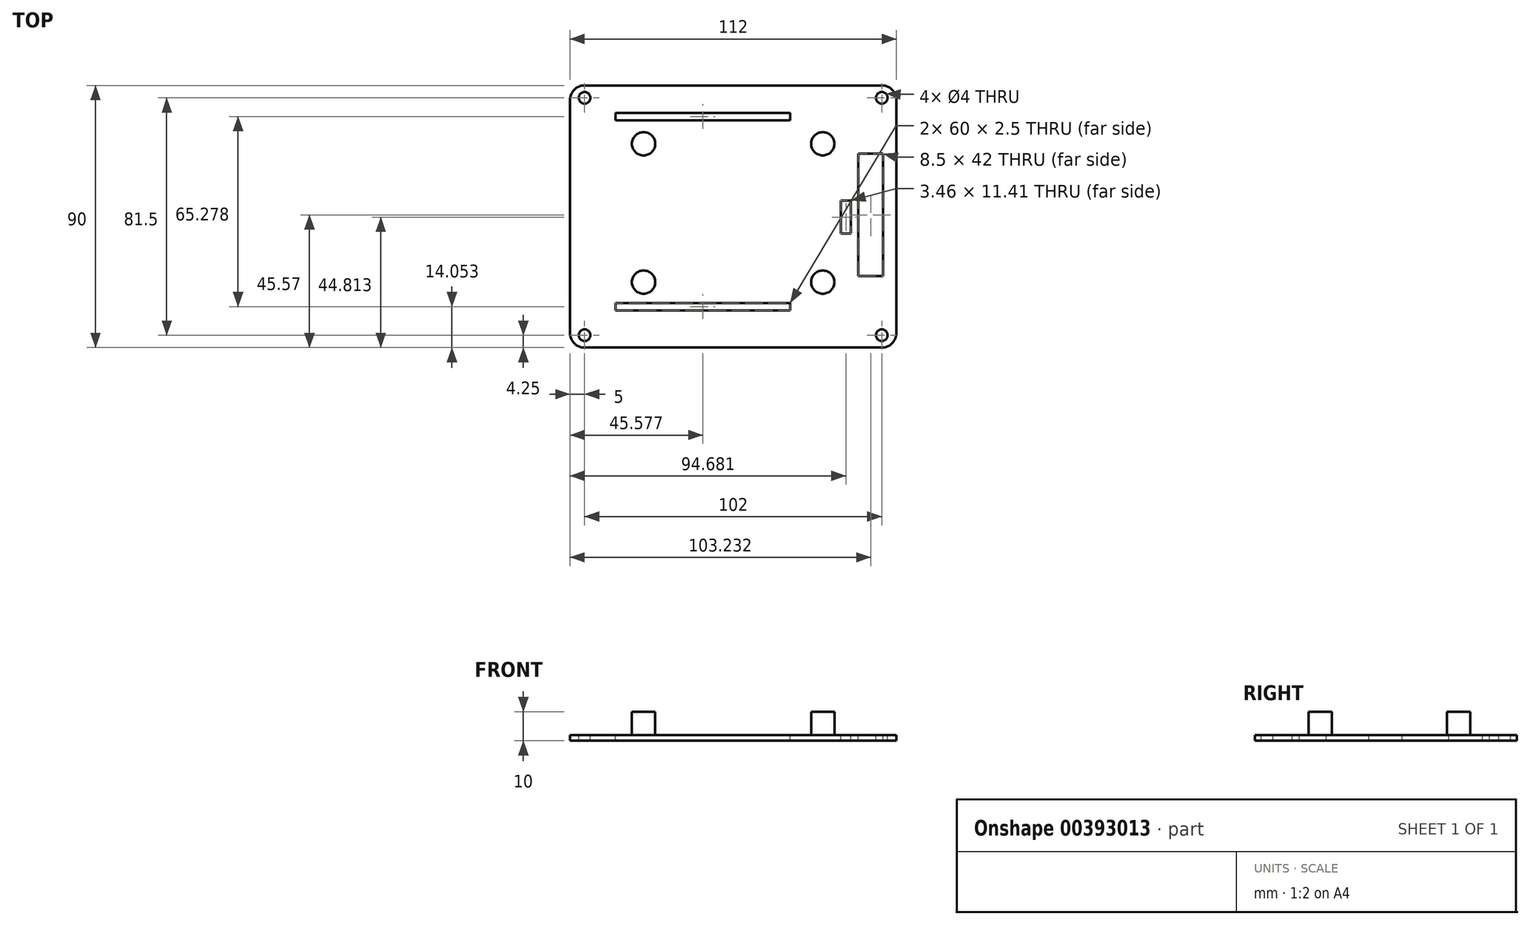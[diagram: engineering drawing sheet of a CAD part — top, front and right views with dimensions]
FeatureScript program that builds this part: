
annotation { "Feature Type Name" : "Feature", "Feature Type Description" : "" }
export const myFeature = defineFeature(function(context is Context, id is Id, definition is map)
    precondition{}
    {
        {
            var Q0;
            Q0=qCreatedBy(makeId("Top.planeOp"),FACE);
            var sketch = newSketch(context, id + "F0", { "sketchPlane" : qUnion([Q0])});
            skLineSegment(sketch, "E0.bottom", {"start": v(51, 45) * mm, "end": v(-51, 45) * mm});
            skLineSegment(sketch, "E0.top", {"start": v(51, -45) * mm, "end": v(-51, -45) * mm});
            skLineSegment(sketch, "E0.left", {"start": v(56, 40) * mm, "end": v(56, -40) * mm});
            skLineSegment(sketch, "E0.right", {"start": v(-56, 40) * mm, "end": v(-56, -40) * mm});
            skPoint(sketch, "E0.middle", {"position": v(0, 0) * mm});
            skPoint(sketch, "E1.visualSharp", {"position": v(56, 45) * mm});
            skArc(sketch, "E1.filletArc", {"start": v(56, 40) * mm, "mid": v(54.54, 43.54) * mm, "end": v(51, 45) * mm});
            skPoint(sketch, "E2.visualSharp", {"position": v(56, -45) * mm});
            skArc(sketch, "E2.filletArc", {"start": v(51, -45) * mm, "mid": v(54.54, -43.54) * mm, "end": v(56, -40) * mm});
            skPoint(sketch, "E3.visualSharp", {"position": v(-56, -45) * mm});
            skArc(sketch, "E3.filletArc", {"start": v(-56, -40) * mm, "mid": v(-54.54, -43.54) * mm, "end": v(-51, -45) * mm});
            skPoint(sketch, "E4.visualSharp", {"position": v(-56, 45) * mm});
            skArc(sketch, "E4.filletArc", {"start": v(-51, 45) * mm, "mid": v(-54.54, 43.54) * mm, "end": v(-56, 40) * mm});
            skSolve(sketch);
        }
        {
            var Q0;
            Q0 = qSketchRegion(id + "F0", true);
            extrude(context, id + "F1", {"entities" : qUnion([Q0]), "depth" : 2 * mm, "offsetDistance" : 25 * mm});
        }
        {
            var Q0;
            Q0=makeQuery(id+"F1.opExtrude","CAP_FACE",FACE,{"disambiguationData":[OSD([sQuery(id+"F0.wireOp",EDGE,"E0.bottom"),sQuery(id+"F0.wireOp",EDGE,"E0.top"),sQuery(id+"F0.wireOp",EDGE,"E0.left"),sQuery(id+"F0.wireOp",EDGE,"E0.right"),sQuery(id+"F0.wireOp",EDGE,"E1.filletArc"),sQuery(id+"F0.wireOp",EDGE,"E2.filletArc"),sQuery(id+"F0.wireOp",EDGE,"E3.filletArc"),sQuery(id+"F0.wireOp",EDGE,"E4.filletArc")])],"isStart":false});
            var sketch = newSketch(context, id + "F2", { "sketchPlane" : qUnion([Q0])});
            skLineSegment(sketch, "E5.bottom", {"start": v(42.98, 21.57) * mm, "end": v(51.48, 21.57) * mm});
            skLineSegment(sketch, "E5.top", {"start": v(42.98, -20.43) * mm, "end": v(51.48, -20.43) * mm});
            skLineSegment(sketch, "E5.left", {"start": v(42.98, 21.57) * mm, "end": v(42.98, -20.43) * mm});
            skLineSegment(sketch, "E5.right", {"start": v(51.48, 21.57) * mm, "end": v(51.48, -20.43) * mm});
            skSolve(sketch);
        }
        {
            var Q0;
            Q0 = qSketchRegion(id + "F2", true);
            extrude(context, id + "F3", {"entities" : qUnion([Q0]), "operationType" : NewBodyOperationType.REMOVE, "oppositeDirection" : true, "depth" : 25 * mm, "offsetDistance" : 25 * mm});
        }
        {
            var Q0;
            Q0=makeQuery(id+"F1.opExtrude","CAP_FACE",FACE,{"disambiguationData":[OSD([sQuery(id+"F0.wireOp",EDGE,"E0.bottom"),sQuery(id+"F0.wireOp",EDGE,"E0.top"),sQuery(id+"F0.wireOp",EDGE,"E0.left"),sQuery(id+"F0.wireOp",EDGE,"E0.right"),sQuery(id+"F0.wireOp",EDGE,"E1.filletArc"),sQuery(id+"F0.wireOp",EDGE,"E2.filletArc"),sQuery(id+"F0.wireOp",EDGE,"E3.filletArc"),sQuery(id+"F0.wireOp",EDGE,"E4.filletArc")])],"isStart":false});
            var sketch = newSketch(context, id + "F4", { "sketchPlane" : qUnion([Q0])});
            skLineSegment(sketch, "E6.bottom", {"start": v(51, 40.75) * mm, "end": v(-51, 40.75) * mm});
            skLineSegment(sketch, "E6.top", {"start": v(51, -40.75) * mm, "end": v(-51, -40.75) * mm});
            skLineSegment(sketch, "E6.left", {"start": v(51, 40.75) * mm, "end": v(51, -40.75) * mm});
            skLineSegment(sketch, "E6.right", {"start": v(-51, 40.75) * mm, "end": v(-51, -40.75) * mm});
            skPoint(sketch, "E6.middle", {"position": v(0, 0) * mm});
            skCircle(sketch, "E7", {"center": v(-51, 40.75) * mm, "radius": 2 * mm});
            skCircle(sketch, "E8", {"center": v(51, 40.75) * mm, "radius": 2 * mm});
            skCircle(sketch, "E9", {"center": v(51, -40.75) * mm, "radius": 2 * mm});
            skCircle(sketch, "E10", {"center": v(-51, -40.75) * mm, "radius": 2 * mm});
            skSolve(sketch);
        }
        {
            var Q0;
            Q0=makeQuery(id+"F4.imprint","IMPRINT",FACE,{"disambiguationData":[TD([[makeQuery(id+"F4.imprint","IMPRINT",EDGE,{"derivedFrom":makeQuery(id+"F3.boolean.opBoolean","COPY",EDGE,{"derivedFrom":makeQuery(id+"F3.opExtrude","CAP_EDGE",EDGE,{"disambiguationData":[OSD([sQuery(id+"F2.wireOp",EDGE,"E5.bottom")])],"isStart":true})})}),-1.0]])]});
            var Q1;
            {var subQ0=sQuery(id+"F4.wireOp",EDGE,"E6.left");var subQ1=sQuery(id+"F4.wireOp",EDGE,"E6.bottom");var subQ2=makeQuery(id+"F4.imprint","INTERSECT",VERTEX,{"derivedFrom":[subQ1,subQ0]});Q1=makeQuery(id+"F4.imprint","IMPRINT",FACE,{"disambiguationData":[TD([[makeQuery(id+"F4.imprint","IMPRINT",EDGE,{"disambiguationData":[TD([[subQ2,-1.0]])],"derivedFrom":subQ1}),1.0]])]});}
            var Q2;
            {var subQ0=sQuery(id+"F4.wireOp",EDGE,"E6.left");var subQ1=sQuery(id+"F4.wireOp",EDGE,"E6.bottom");var subQ2=makeQuery(id+"F4.imprint","INTERSECT",VERTEX,{"derivedFrom":[subQ1,subQ0]});Q2=makeQuery(id+"F4.imprint","IMPRINT",FACE,{"disambiguationData":[TD([[makeQuery(id+"F4.imprint","IMPRINT",EDGE,{"disambiguationData":[TD([[subQ2,-1.0]])],"derivedFrom":subQ1}),-1.0]])]});}
            var Q3;
            {var subQ0=sQuery(id+"F4.wireOp",EDGE,"E6.right");var subQ1=sQuery(id+"F4.wireOp",EDGE,"E6.bottom");var subQ2=makeQuery(id+"F4.imprint","INTERSECT",VERTEX,{"derivedFrom":[subQ1,subQ0]});Q3=makeQuery(id+"F4.imprint","IMPRINT",FACE,{"disambiguationData":[TD([[makeQuery(id+"F4.imprint","IMPRINT",EDGE,{"disambiguationData":[TD([[subQ2,1.0]])],"derivedFrom":subQ1}),-1.0]])]});}
            var Q4;
            {var subQ0=sQuery(id+"F4.wireOp",EDGE,"E6.right");var subQ1=sQuery(id+"F4.wireOp",EDGE,"E6.bottom");var subQ2=makeQuery(id+"F4.imprint","INTERSECT",VERTEX,{"derivedFrom":[subQ1,subQ0]});Q4=makeQuery(id+"F4.imprint","IMPRINT",FACE,{"disambiguationData":[TD([[makeQuery(id+"F4.imprint","IMPRINT",EDGE,{"disambiguationData":[TD([[subQ2,1.0]])],"derivedFrom":subQ1}),1.0]])]});}
            var Q5;
            {var subQ0=sQuery(id+"F4.wireOp",EDGE,"E6.left");var subQ1=sQuery(id+"F4.wireOp",EDGE,"E6.top");var subQ2=makeQuery(id+"F4.imprint","INTERSECT",VERTEX,{"derivedFrom":[subQ1,subQ0]});Q5=makeQuery(id+"F4.imprint","IMPRINT",FACE,{"disambiguationData":[TD([[makeQuery(id+"F4.imprint","IMPRINT",EDGE,{"disambiguationData":[TD([[subQ2,-1.0]])],"derivedFrom":subQ1}),-1.0]])]});}
            var Q6;
            {var subQ0=sQuery(id+"F4.wireOp",EDGE,"E6.left");var subQ1=sQuery(id+"F4.wireOp",EDGE,"E6.top");var subQ2=makeQuery(id+"F4.imprint","INTERSECT",VERTEX,{"derivedFrom":[subQ1,subQ0]});Q6=makeQuery(id+"F4.imprint","IMPRINT",FACE,{"disambiguationData":[TD([[makeQuery(id+"F4.imprint","IMPRINT",EDGE,{"disambiguationData":[TD([[subQ2,-1.0]])],"derivedFrom":subQ1}),1.0]])]});}
            var Q7;
            {var subQ0=sQuery(id+"F4.wireOp",EDGE,"E6.right");var subQ1=sQuery(id+"F4.wireOp",EDGE,"E6.top");var subQ2=makeQuery(id+"F4.imprint","INTERSECT",VERTEX,{"derivedFrom":[subQ1,subQ0]});Q7=makeQuery(id+"F4.imprint","IMPRINT",FACE,{"disambiguationData":[TD([[makeQuery(id+"F4.imprint","IMPRINT",EDGE,{"disambiguationData":[TD([[subQ2,1.0]])],"derivedFrom":subQ1}),-1.0]])]});}
            var Q8;
            {var subQ0=sQuery(id+"F4.wireOp",EDGE,"E6.right");var subQ1=sQuery(id+"F4.wireOp",EDGE,"E6.top");var subQ2=makeQuery(id+"F4.imprint","INTERSECT",VERTEX,{"derivedFrom":[subQ1,subQ0]});Q8=makeQuery(id+"F4.imprint","IMPRINT",FACE,{"disambiguationData":[TD([[makeQuery(id+"F4.imprint","IMPRINT",EDGE,{"disambiguationData":[TD([[subQ2,1.0]])],"derivedFrom":subQ1}),1.0]])]});}
            extrude(context, id + "F5", {"entities" : qUnion([Q0, Q1, Q2, Q3, Q4, Q5, Q6, Q7, Q8]), "operationType" : NewBodyOperationType.REMOVE, "oppositeDirection" : true, "depth" : 25 * mm, "offsetDistance" : 25 * mm});
        }
        {
            var Q0;
            Q0=makeQuery(id+"F1.opExtrude","CAP_FACE",FACE,{"disambiguationData":[OSD([sQuery(id+"F0.wireOp",EDGE,"E0.bottom"),sQuery(id+"F0.wireOp",EDGE,"E0.top"),sQuery(id+"F0.wireOp",EDGE,"E0.left"),sQuery(id+"F0.wireOp",EDGE,"E0.right"),sQuery(id+"F0.wireOp",EDGE,"E1.filletArc"),sQuery(id+"F0.wireOp",EDGE,"E2.filletArc"),sQuery(id+"F0.wireOp",EDGE,"E3.filletArc"),sQuery(id+"F0.wireOp",EDGE,"E4.filletArc")])],"isStart":false});
            var sketch = newSketch(context, id + "F6", { "sketchPlane" : qUnion([Q0])});
            skLineSegment(sketch, "E11.bottom", {"start": v(-40.42, 35.58) * mm, "end": v(19.58, 35.58) * mm});
            skLineSegment(sketch, "E11.top", {"start": v(-40.42, 33.08) * mm, "end": v(19.58, 33.08) * mm});
            skLineSegment(sketch, "E11.left", {"start": v(-40.42, 35.58) * mm, "end": v(-40.42, 33.08) * mm});
            skLineSegment(sketch, "E11.right", {"start": v(19.58, 35.58) * mm, "end": v(19.58, 33.08) * mm});
            skLineSegment(sketch, "E12.bottom", {"start": v(-40.42, -29.7) * mm, "end": v(19.58, -29.7) * mm});
            skLineSegment(sketch, "E12.top", {"start": v(-40.42, -32.2) * mm, "end": v(19.58, -32.2) * mm});
            skLineSegment(sketch, "E12.left", {"start": v(-40.42, -29.7) * mm, "end": v(-40.42, -32.2) * mm});
            skLineSegment(sketch, "E12.right", {"start": v(19.58, -29.7) * mm, "end": v(19.58, -32.2) * mm});
            skSolve(sketch);
        }
        {
            var Q0;
            Q0 = qSketchRegion(id + "F6", true);
            extrude(context, id + "F7", {"entities" : qUnion([Q0]), "operationType" : NewBodyOperationType.REMOVE, "oppositeDirection" : true, "depth" : 25 * mm, "offsetDistance" : 25 * mm});
        }
        {
            var Q0;
            Q0=makeQuery(id+"F1.opExtrude","CAP_FACE",FACE,{"disambiguationData":[OSD([sQuery(id+"F0.wireOp",EDGE,"E0.bottom"),sQuery(id+"F0.wireOp",EDGE,"E0.top"),sQuery(id+"F0.wireOp",EDGE,"E0.left"),sQuery(id+"F0.wireOp",EDGE,"E0.right"),sQuery(id+"F0.wireOp",EDGE,"E1.filletArc"),sQuery(id+"F0.wireOp",EDGE,"E2.filletArc"),sQuery(id+"F0.wireOp",EDGE,"E3.filletArc"),sQuery(id+"F0.wireOp",EDGE,"E4.filletArc")])],"isStart":false});
            var sketch = newSketch(context, id + "F8", { "sketchPlane" : qUnion([Q0])});
            skLineSegment(sketch, "E13.bottom", {"start": v(-30.75, -22.53) * mm, "end": v(30.75, -22.53) * mm});
            skLineSegment(sketch, "E13.top", {"start": v(-30.75, 24.97) * mm, "end": v(30.75, 24.97) * mm});
            skLineSegment(sketch, "E13.left", {"start": v(-30.75, -22.53) * mm, "end": v(-30.75, 24.97) * mm});
            skLineSegment(sketch, "E13.right", {"start": v(30.75, -22.53) * mm, "end": v(30.75, 24.97) * mm});
            skCircle(sketch, "E14", {"center": v(-30.75, 24.97) * mm, "radius": 4 * mm});
            skCircle(sketch, "E15", {"center": v(30.75, 24.97) * mm, "radius": 4 * mm});
            skCircle(sketch, "E16", {"center": v(30.75, -22.53) * mm, "radius": 4 * mm});
            skCircle(sketch, "E17", {"center": v(-30.75, -22.53) * mm, "radius": 4 * mm});
            skSolve(sketch);
        }
        {
            var Q0;
            {var subQ0=sQuery(id+"F8.wireOp",EDGE,"E13.left");var subQ1=sQuery(id+"F8.wireOp",EDGE,"E13.bottom");var subQ2=makeQuery(id+"F8.imprint","INTERSECT",VERTEX,{"derivedFrom":[subQ1,subQ0]});Q0=makeQuery(id+"F8.imprint","IMPRINT",FACE,{"disambiguationData":[TD([[makeQuery(id+"F8.imprint","IMPRINT",EDGE,{"disambiguationData":[TD([[subQ2,-1.0]])],"derivedFrom":subQ1}),1.0]])]});}
            var Q1;
            {var subQ0=sQuery(id+"F8.wireOp",EDGE,"E13.left");var subQ1=sQuery(id+"F8.wireOp",EDGE,"E13.bottom");var subQ2=makeQuery(id+"F8.imprint","INTERSECT",VERTEX,{"derivedFrom":[subQ1,subQ0]});Q1=makeQuery(id+"F8.imprint","IMPRINT",FACE,{"disambiguationData":[TD([[makeQuery(id+"F8.imprint","IMPRINT",EDGE,{"disambiguationData":[TD([[subQ2,-1.0]])],"derivedFrom":subQ1}),-1.0]])]});}
            var Q2;
            {var subQ0=sQuery(id+"F8.wireOp",EDGE,"E13.right");var subQ1=sQuery(id+"F8.wireOp",EDGE,"E13.bottom");var subQ2=makeQuery(id+"F8.imprint","INTERSECT",VERTEX,{"derivedFrom":[subQ1,subQ0]});Q2=makeQuery(id+"F8.imprint","IMPRINT",FACE,{"disambiguationData":[TD([[makeQuery(id+"F8.imprint","IMPRINT",EDGE,{"disambiguationData":[TD([[subQ2,1.0]])],"derivedFrom":subQ1}),1.0]])]});}
            var Q3;
            {var subQ0=sQuery(id+"F8.wireOp",EDGE,"E13.right");var subQ1=sQuery(id+"F8.wireOp",EDGE,"E13.bottom");var subQ2=makeQuery(id+"F8.imprint","INTERSECT",VERTEX,{"derivedFrom":[subQ1,subQ0]});Q3=makeQuery(id+"F8.imprint","IMPRINT",FACE,{"disambiguationData":[TD([[makeQuery(id+"F8.imprint","IMPRINT",EDGE,{"disambiguationData":[TD([[subQ2,1.0]])],"derivedFrom":subQ1}),-1.0]])]});}
            var Q4;
            {var subQ0=sQuery(id+"F8.wireOp",EDGE,"E13.left");var subQ1=sQuery(id+"F8.wireOp",EDGE,"E13.top");var subQ2=makeQuery(id+"F8.imprint","INTERSECT",VERTEX,{"derivedFrom":[subQ1,subQ0]});Q4=makeQuery(id+"F8.imprint","IMPRINT",FACE,{"disambiguationData":[TD([[makeQuery(id+"F8.imprint","IMPRINT",EDGE,{"disambiguationData":[TD([[subQ2,-1.0]])],"derivedFrom":subQ1}),1.0]])]});}
            var Q5;
            {var subQ0=sQuery(id+"F8.wireOp",EDGE,"E13.left");var subQ1=sQuery(id+"F8.wireOp",EDGE,"E13.top");var subQ2=makeQuery(id+"F8.imprint","INTERSECT",VERTEX,{"derivedFrom":[subQ1,subQ0]});Q5=makeQuery(id+"F8.imprint","IMPRINT",FACE,{"disambiguationData":[TD([[makeQuery(id+"F8.imprint","IMPRINT",EDGE,{"disambiguationData":[TD([[subQ2,-1.0]])],"derivedFrom":subQ1}),-1.0]])]});}
            var Q6;
            {var subQ0=sQuery(id+"F8.wireOp",EDGE,"E13.right");var subQ1=sQuery(id+"F8.wireOp",EDGE,"E13.top");var subQ2=makeQuery(id+"F8.imprint","INTERSECT",VERTEX,{"derivedFrom":[subQ1,subQ0]});Q6=makeQuery(id+"F8.imprint","IMPRINT",FACE,{"disambiguationData":[TD([[makeQuery(id+"F8.imprint","IMPRINT",EDGE,{"disambiguationData":[TD([[subQ2,1.0]])],"derivedFrom":subQ1}),-1.0]])]});}
            var Q7;
            {var subQ0=sQuery(id+"F8.wireOp",EDGE,"E13.right");var subQ1=sQuery(id+"F8.wireOp",EDGE,"E13.top");var subQ2=makeQuery(id+"F8.imprint","INTERSECT",VERTEX,{"derivedFrom":[subQ1,subQ0]});Q7=makeQuery(id+"F8.imprint","IMPRINT",FACE,{"disambiguationData":[TD([[makeQuery(id+"F8.imprint","IMPRINT",EDGE,{"disambiguationData":[TD([[subQ2,1.0]])],"derivedFrom":subQ1}),1.0]])]});}
            extrude(context, id + "F9", {"entities" : qUnion([Q0, Q1, Q2, Q3, Q4, Q5, Q6, Q7]), "operationType" : NewBodyOperationType.ADD, "depth" : 8 * mm, "offsetDistance" : 25 * mm});
        }
        {
            var Q0;
            Q0=makeQuery(id+"F1.opExtrude","CAP_FACE",FACE,{"disambiguationData":[OSD([sQuery(id+"F0.wireOp",EDGE,"E0.bottom"),sQuery(id+"F0.wireOp",EDGE,"E0.top"),sQuery(id+"F0.wireOp",EDGE,"E0.left"),sQuery(id+"F0.wireOp",EDGE,"E0.right"),sQuery(id+"F0.wireOp",EDGE,"E1.filletArc"),sQuery(id+"F0.wireOp",EDGE,"E2.filletArc"),sQuery(id+"F0.wireOp",EDGE,"E3.filletArc"),sQuery(id+"F0.wireOp",EDGE,"E4.filletArc")])],"isStart":false});
            var sketch = newSketch(context, id + "F10", { "sketchPlane" : qUnion([Q0])});
            skLineSegment(sketch, "E18.bottom", {"start": v(40.41, -5.9) * mm, "end": v(36.95, -5.9) * mm});
            skLineSegment(sketch, "E18.top", {"start": v(40.41, 5.52) * mm, "end": v(36.95, 5.52) * mm});
            skLineSegment(sketch, "E18.left", {"start": v(40.41, -5.9) * mm, "end": v(40.41, 5.52) * mm});
            skLineSegment(sketch, "E18.right", {"start": v(36.95, -5.9) * mm, "end": v(36.95, 5.52) * mm});
            skSolve(sketch);
        }
        {
            var Q0;
            Q0 = qSketchRegion(id + "F10", true);
            extrude(context, id + "F11", {"entities" : qUnion([Q0]), "operationType" : NewBodyOperationType.REMOVE, "oppositeDirection" : true, "depth" : 25 * mm, "offsetDistance" : 25 * mm});
        }
    });
